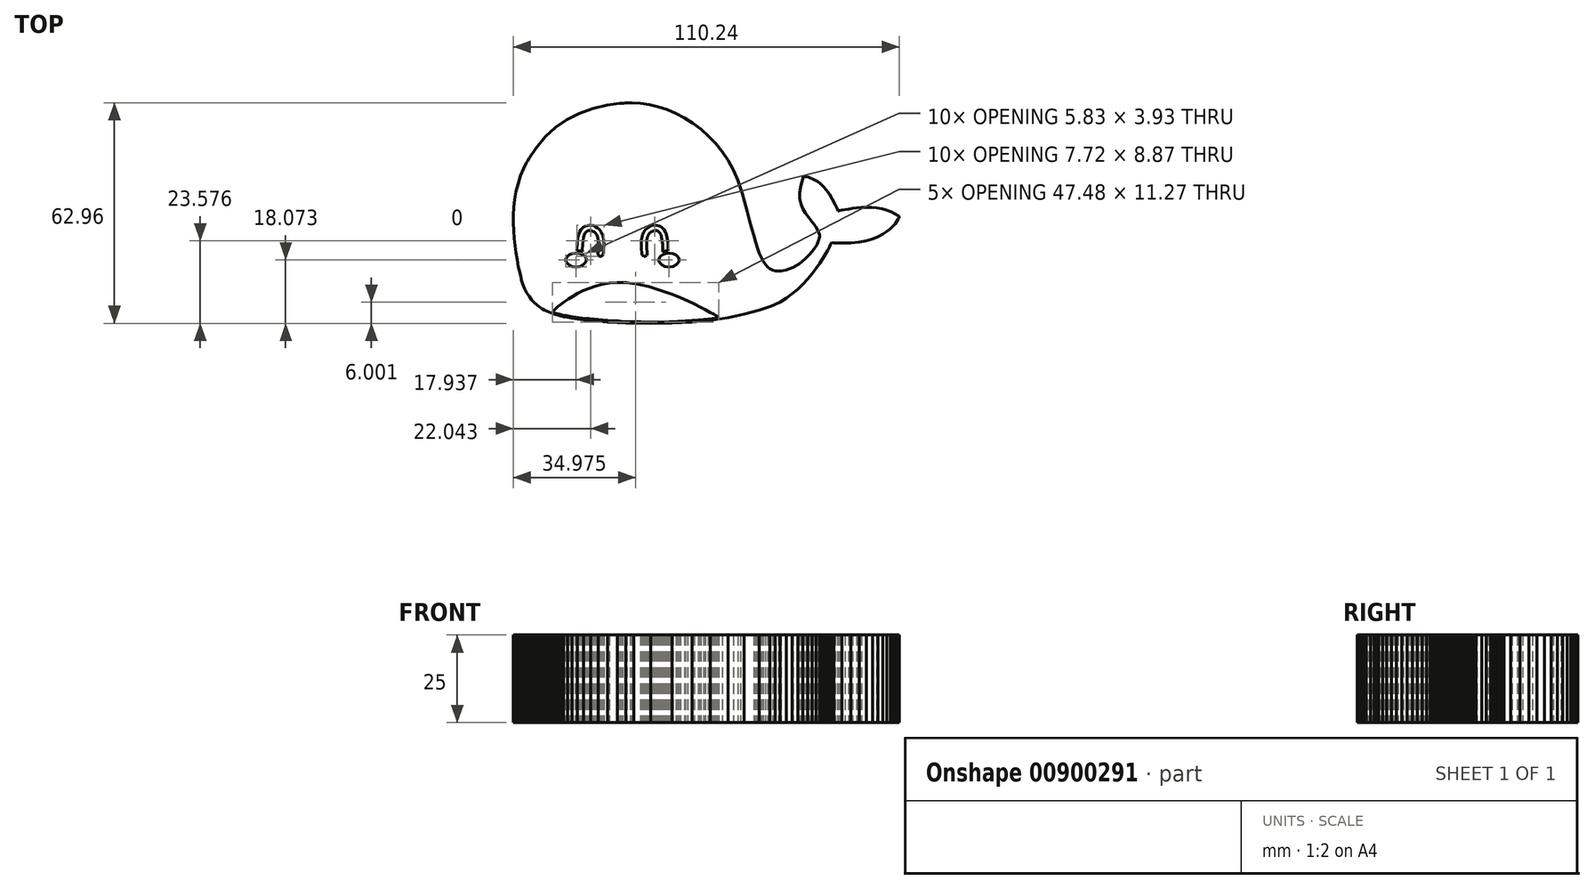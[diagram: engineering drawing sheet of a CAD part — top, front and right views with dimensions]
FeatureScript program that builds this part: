
annotation { "Feature Type Name" : "Feature", "Feature Type Description" : "" }
export const myFeature = defineFeature(function(context is Context, id is Id, definition is map)
    precondition{}
    {
        {
            var Q0;
            Q0=qCreatedBy(makeId("Top.planeOp"),FACE);
            var sketch = newSketch(context, id + "F0", { "sketchPlane" : qUnion([Q0])});
            skLineSegment(sketch, "E0", {"start": v(-43.89, -35.84) * mm, "end": v(-43.96, -35.82) * mm});
            skLineSegment(sketch, "E1", {"start": v(-43.96, -35.82) * mm, "end": v(-44.19, -35.76) * mm});
            skLineSegment(sketch, "E2", {"start": v(-44.19, -35.76) * mm, "end": v(-44.54, -35.65) * mm});
            skLineSegment(sketch, "E3", {"start": v(-44.54, -35.65) * mm, "end": v(-45, -35.48) * mm});
            skLineSegment(sketch, "E4", {"start": v(-45, -35.48) * mm, "end": v(-45.55, -35.25) * mm});
            skLineSegment(sketch, "E5", {"start": v(-45.55, -35.25) * mm, "end": v(-46.18, -34.93) * mm});
            skLineSegment(sketch, "E6", {"start": v(-46.18, -34.93) * mm, "end": v(-46.87, -34.54) * mm});
            skLineSegment(sketch, "E7", {"start": v(-46.87, -34.54) * mm, "end": v(-47.6, -34.06) * mm});
            skLineSegment(sketch, "E8", {"start": v(-47.6, -34.06) * mm, "end": v(-48.35, -33.47) * mm});
            skLineSegment(sketch, "E9", {"start": v(-48.35, -33.47) * mm, "end": v(-49.11, -32.78) * mm});
            skLineSegment(sketch, "E10", {"start": v(-49.11, -32.78) * mm, "end": v(-49.86, -31.97) * mm});
            skLineSegment(sketch, "E11", {"start": v(-49.86, -31.97) * mm, "end": v(-50.59, -31.03) * mm});
            skLineSegment(sketch, "E12", {"start": v(-50.59, -31.03) * mm, "end": v(-51.27, -29.97) * mm});
            skLineSegment(sketch, "E13", {"start": v(-51.27, -29.97) * mm, "end": v(-51.89, -28.76) * mm});
            skLineSegment(sketch, "E14", {"start": v(-51.89, -28.76) * mm, "end": v(-52.43, -27.4) * mm});
            skLineSegment(sketch, "E15", {"start": v(-52.43, -27.4) * mm, "end": v(-52.78, -26.28) * mm});
            skLineSegment(sketch, "E16", {"start": v(-52.78, -26.28) * mm, "end": v(-52.87, -25.9) * mm});
            skLineSegment(sketch, "E17", {"start": v(-52.87, -25.9) * mm, "end": v(-52.97, -25.48) * mm});
            skLineSegment(sketch, "E18", {"start": v(-52.97, -25.48) * mm, "end": v(-53.26, -24.24) * mm});
            skLineSegment(sketch, "E19", {"start": v(-53.26, -24.24) * mm, "end": v(-53.65, -22.46) * mm});
            skLineSegment(sketch, "E20", {"start": v(-53.65, -22.46) * mm, "end": v(-54.02, -20.58) * mm});
            skLineSegment(sketch, "E21", {"start": v(-54.02, -20.58) * mm, "end": v(-54.36, -18.6) * mm});
            skLineSegment(sketch, "E22", {"start": v(-54.36, -18.6) * mm, "end": v(-54.65, -16.55) * mm});
            skLineSegment(sketch, "E23", {"start": v(-54.65, -16.55) * mm, "end": v(-54.88, -14.43) * mm});
            skLineSegment(sketch, "E24", {"start": v(-54.88, -14.43) * mm, "end": v(-55.04, -12.26) * mm});
            skLineSegment(sketch, "E25", {"start": v(-55.04, -12.26) * mm, "end": v(-55.12, -10.05) * mm});
            skLineSegment(sketch, "E26", {"start": v(-55.12, -10.05) * mm, "end": v(-55.1, -7.8) * mm});
            skLineSegment(sketch, "E27", {"start": v(-55.1, -7.8) * mm, "end": v(-54.96, -5.55) * mm});
            skLineSegment(sketch, "E28", {"start": v(-54.96, -5.55) * mm, "end": v(-54.7, -3.3) * mm});
            skLineSegment(sketch, "E29", {"start": v(-54.7, -3.3) * mm, "end": v(-54.32, -1.05) * mm});
            skLineSegment(sketch, "E30", {"start": v(-54.32, -1.05) * mm, "end": v(-53.77, 1.17) * mm});
            skLineSegment(sketch, "E31", {"start": v(-53.77, 1.17) * mm, "end": v(-53.06, 3.35) * mm});
            skLineSegment(sketch, "E32", {"start": v(-53.06, 3.35) * mm, "end": v(-52.18, 5.48) * mm});
            skLineSegment(sketch, "E33", {"start": v(-52.18, 5.48) * mm, "end": v(-51.4, 7.05) * mm});
            skLineSegment(sketch, "E34", {"start": v(-51.4, 7.05) * mm, "end": v(-51.1, 7.55) * mm});
            skLineSegment(sketch, "E35", {"start": v(-51.1, 7.55) * mm, "end": v(-50.54, 8.52) * mm});
            skLineSegment(sketch, "E36", {"start": v(-50.54, 8.52) * mm, "end": v(-48.66, 11.33) * mm});
            skLineSegment(sketch, "E37", {"start": v(-48.66, 11.33) * mm, "end": v(-45.98, 14.55) * mm});
            skLineSegment(sketch, "E38", {"start": v(-45.98, 14.55) * mm, "end": v(-43.05, 17.26) * mm});
            skLineSegment(sketch, "E39", {"start": v(-43.05, 17.26) * mm, "end": v(-39.84, 19.48) * mm});
            skLineSegment(sketch, "E40", {"start": v(-39.84, 19.48) * mm, "end": v(-36.32, 21.24) * mm});
            skLineSegment(sketch, "E41", {"start": v(-36.32, 21.24) * mm, "end": v(-32.47, 22.6) * mm});
            skLineSegment(sketch, "E42", {"start": v(-32.47, 22.6) * mm, "end": v(-28.27, 23.55) * mm});
            skLineSegment(sketch, "E43", {"start": v(-28.27, 23.55) * mm, "end": v(-24.82, 24.06) * mm});
            skLineSegment(sketch, "E44", {"start": v(-24.82, 24.06) * mm, "end": v(-23.67, 24.16) * mm});
            skLineSegment(sketch, "E45", {"start": v(-23.67, 24.16) * mm, "end": v(-23.07, 24.22) * mm});
            skLineSegment(sketch, "E46", {"start": v(-23.07, 24.22) * mm, "end": v(-21.23, 24.26) * mm});
            skLineSegment(sketch, "E47", {"start": v(-21.23, 24.26) * mm, "end": v(-18.74, 24.12) * mm});
            skLineSegment(sketch, "E48", {"start": v(-18.74, 24.12) * mm, "end": v(-16.21, 23.74) * mm});
            skLineSegment(sketch, "E49", {"start": v(-16.21, 23.74) * mm, "end": v(-13.67, 23.12) * mm});
            skLineSegment(sketch, "E50", {"start": v(-13.67, 23.12) * mm, "end": v(-11.14, 22.28) * mm});
            skLineSegment(sketch, "E51", {"start": v(-11.14, 22.28) * mm, "end": v(-8.64, 21.2) * mm});
            skLineSegment(sketch, "E52", {"start": v(-8.64, 21.2) * mm, "end": v(-6.2, 19.92) * mm});
            skLineSegment(sketch, "E53", {"start": v(-6.2, 19.92) * mm, "end": v(-3.82, 18.41) * mm});
            skLineSegment(sketch, "E54", {"start": v(-3.82, 18.41) * mm, "end": v(-1.54, 16.7) * mm});
            skLineSegment(sketch, "E55", {"start": v(-1.54, 16.7) * mm, "end": v(0.63, 14.77) * mm});
            skLineSegment(sketch, "E56", {"start": v(0.63, 14.77) * mm, "end": v(2.66, 12.64) * mm});
            skLineSegment(sketch, "E57", {"start": v(2.66, 12.64) * mm, "end": v(4.53, 10.32) * mm});
            skLineSegment(sketch, "E58", {"start": v(4.53, 10.32) * mm, "end": v(6.22, 7.8) * mm});
            skLineSegment(sketch, "E59", {"start": v(6.22, 7.8) * mm, "end": v(7.72, 5.1) * mm});
            skLineSegment(sketch, "E60", {"start": v(7.72, 5.1) * mm, "end": v(8.99, 2.2) * mm});
            skLineSegment(sketch, "E61", {"start": v(8.99, 2.2) * mm, "end": v(9.8, -0.09) * mm});
            skLineSegment(sketch, "E62", {"start": v(9.8, -0.09) * mm, "end": v(10.02, -0.87) * mm});
            skLineSegment(sketch, "E63", {"start": v(10.02, -0.87) * mm, "end": v(10.24, -1.62) * mm});
            skLineSegment(sketch, "E64", {"start": v(10.24, -1.62) * mm, "end": v(10.87, -3.9) * mm});
            skLineSegment(sketch, "E65", {"start": v(10.87, -3.9) * mm, "end": v(11.64, -6.69) * mm});
            skLineSegment(sketch, "E66", {"start": v(11.64, -6.69) * mm, "end": v(12.33, -9.24) * mm});
            skLineSegment(sketch, "E67", {"start": v(12.33, -9.24) * mm, "end": v(12.96, -11.56) * mm});
            skLineSegment(sketch, "E68", {"start": v(12.96, -11.56) * mm, "end": v(13.55, -13.65) * mm});
            skLineSegment(sketch, "E69", {"start": v(13.55, -13.65) * mm, "end": v(14.1, -15.53) * mm});
            skLineSegment(sketch, "E70", {"start": v(14.1, -15.53) * mm, "end": v(14.63, -17.2) * mm});
            skLineSegment(sketch, "E71", {"start": v(14.63, -17.2) * mm, "end": v(15.15, -18.65) * mm});
            skLineSegment(sketch, "E72", {"start": v(15.15, -18.65) * mm, "end": v(15.69, -19.92) * mm});
            skLineSegment(sketch, "E73", {"start": v(15.69, -19.92) * mm, "end": v(16.24, -20.99) * mm});
            skLineSegment(sketch, "E74", {"start": v(16.24, -20.99) * mm, "end": v(16.83, -21.88) * mm});
            skLineSegment(sketch, "E75", {"start": v(16.83, -21.88) * mm, "end": v(17.47, -22.6) * mm});
            skLineSegment(sketch, "E76", {"start": v(17.47, -22.6) * mm, "end": v(18.16, -23.13) * mm});
            skLineSegment(sketch, "E77", {"start": v(18.16, -23.13) * mm, "end": v(18.94, -23.51) * mm});
            skLineSegment(sketch, "E78", {"start": v(18.94, -23.51) * mm, "end": v(19.8, -23.73) * mm});
            skLineSegment(sketch, "E79", {"start": v(19.8, -23.73) * mm, "end": v(20.53, -23.8) * mm});
            skLineSegment(sketch, "E80", {"start": v(20.53, -23.8) * mm, "end": v(20.77, -23.8) * mm});
            skLineSegment(sketch, "E81", {"start": v(20.77, -23.8) * mm, "end": v(21.28, -23.8) * mm});
            skLineSegment(sketch, "E82", {"start": v(21.28, -23.8) * mm, "end": v(22.8, -23.53) * mm});
            skLineSegment(sketch, "E83", {"start": v(22.8, -23.53) * mm, "end": v(24.75, -22.77) * mm});
            skLineSegment(sketch, "E84", {"start": v(24.75, -22.77) * mm, "end": v(26.57, -21.67) * mm});
            skLineSegment(sketch, "E85", {"start": v(26.57, -21.67) * mm, "end": v(28.22, -20.34) * mm});
            skLineSegment(sketch, "E86", {"start": v(28.22, -20.34) * mm, "end": v(29.64, -18.92) * mm});
            skLineSegment(sketch, "E87", {"start": v(29.64, -18.92) * mm, "end": v(30.78, -17.52) * mm});
            skLineSegment(sketch, "E88", {"start": v(30.78, -17.52) * mm, "end": v(31.58, -16.27) * mm});
            skLineSegment(sketch, "E89", {"start": v(31.58, -16.27) * mm, "end": v(31.93, -15.56) * mm});
            skLineSegment(sketch, "E90", {"start": v(31.93, -15.56) * mm, "end": v(32, -15.3) * mm});
            skLineSegment(sketch, "E91", {"start": v(32, -15.3) * mm, "end": v(32.03, -15.2) * mm});
            skLineSegment(sketch, "E92", {"start": v(32.03, -15.2) * mm, "end": v(32.14, -14.86) * mm});
            skLineSegment(sketch, "E93", {"start": v(32.14, -14.86) * mm, "end": v(32.27, -14.43) * mm});
            skLineSegment(sketch, "E94", {"start": v(32.27, -14.43) * mm, "end": v(32.35, -13.98) * mm});
            skLineSegment(sketch, "E95", {"start": v(32.35, -13.98) * mm, "end": v(32.33, -13.45) * mm});
            skLineSegment(sketch, "E96", {"start": v(32.33, -13.45) * mm, "end": v(32.17, -12.81) * mm});
            skLineSegment(sketch, "E97", {"start": v(32.17, -12.81) * mm, "end": v(31.8, -12.01) * mm});
            skLineSegment(sketch, "E98", {"start": v(31.8, -12.01) * mm, "end": v(31.19, -11.01) * mm});
            skLineSegment(sketch, "E99", {"start": v(31.19, -11.01) * mm, "end": v(30.52, -10.07) * mm});
            skLineSegment(sketch, "E100", {"start": v(30.52, -10.07) * mm, "end": v(30.29, -9.76) * mm});
            skLineSegment(sketch, "E101", {"start": v(30.29, -9.76) * mm, "end": v(30.03, -9.43) * mm});
            skLineSegment(sketch, "E102", {"start": v(30.03, -9.43) * mm, "end": v(29.26, -8.44) * mm});
            skLineSegment(sketch, "E103", {"start": v(29.26, -8.44) * mm, "end": v(28.34, -7.2) * mm});
            skLineSegment(sketch, "E104", {"start": v(28.34, -7.2) * mm, "end": v(27.59, -5.95) * mm});
            skLineSegment(sketch, "E105", {"start": v(27.59, -5.95) * mm, "end": v(27.03, -4.62) * mm});
            skLineSegment(sketch, "E106", {"start": v(27.03, -4.62) * mm, "end": v(26.72, -3.12) * mm});
            skLineSegment(sketch, "E107", {"start": v(26.72, -3.12) * mm, "end": v(26.7, -1.38) * mm});
            skLineSegment(sketch, "E108", {"start": v(26.7, -1.38) * mm, "end": v(27.02, 0.7) * mm});
            skLineSegment(sketch, "E109", {"start": v(27.02, 0.7) * mm, "end": v(27.52, 2.57) * mm});
            skLineSegment(sketch, "E110", {"start": v(27.52, 2.57) * mm, "end": v(27.72, 3.19) * mm});
            skLineSegment(sketch, "E111", {"start": v(27.72, 3.19) * mm, "end": v(27.79, 3.2) * mm});
            skLineSegment(sketch, "E112", {"start": v(27.79, 3.2) * mm, "end": v(27.98, 3.2) * mm});
            skLineSegment(sketch, "E113", {"start": v(27.98, 3.2) * mm, "end": v(28.28, 3.18) * mm});
            skLineSegment(sketch, "E114", {"start": v(28.28, 3.18) * mm, "end": v(28.69, 3.12) * mm});
            skLineSegment(sketch, "E115", {"start": v(28.69, 3.12) * mm, "end": v(29.19, 3.02) * mm});
            skLineSegment(sketch, "E116", {"start": v(29.19, 3.02) * mm, "end": v(29.76, 2.84) * mm});
            skLineSegment(sketch, "E117", {"start": v(29.76, 2.84) * mm, "end": v(30.41, 2.57) * mm});
            skLineSegment(sketch, "E118", {"start": v(30.41, 2.57) * mm, "end": v(31.12, 2.2) * mm});
            skLineSegment(sketch, "E119", {"start": v(31.12, 2.2) * mm, "end": v(31.88, 1.7) * mm});
            skLineSegment(sketch, "E120", {"start": v(31.88, 1.7) * mm, "end": v(32.67, 1.07) * mm});
            skLineSegment(sketch, "E121", {"start": v(32.67, 1.07) * mm, "end": v(33.5, 0.28) * mm});
            skLineSegment(sketch, "E122", {"start": v(33.5, 0.28) * mm, "end": v(34.33, -0.69) * mm});
            skLineSegment(sketch, "E123", {"start": v(34.33, -0.69) * mm, "end": v(35.17, -1.84) * mm});
            skLineSegment(sketch, "E124", {"start": v(35.17, -1.84) * mm, "end": v(36, -3.2) * mm});
            skLineSegment(sketch, "E125", {"start": v(36, -3.2) * mm, "end": v(36.82, -4.8) * mm});
            skLineSegment(sketch, "E126", {"start": v(36.82, -4.8) * mm, "end": v(37.43, -6.17) * mm});
            skLineSegment(sketch, "E127", {"start": v(37.43, -6.17) * mm, "end": v(37.61, -6.63) * mm});
            skLineSegment(sketch, "E128", {"start": v(37.61, -6.63) * mm, "end": v(37.75, -6.6) * mm});
            skLineSegment(sketch, "E129", {"start": v(37.75, -6.6) * mm, "end": v(38.14, -6.5) * mm});
            skLineSegment(sketch, "E130", {"start": v(38.14, -6.5) * mm, "end": v(38.77, -6.37) * mm});
            skLineSegment(sketch, "E131", {"start": v(38.77, -6.37) * mm, "end": v(39.59, -6.22) * mm});
            skLineSegment(sketch, "E132", {"start": v(39.59, -6.22) * mm, "end": v(40.58, -6.05) * mm});
            skLineSegment(sketch, "E133", {"start": v(40.58, -6.05) * mm, "end": v(41.73, -5.9) * mm});
            skLineSegment(sketch, "E134", {"start": v(41.73, -5.9) * mm, "end": v(42.99, -5.76) * mm});
            skLineSegment(sketch, "E135", {"start": v(42.99, -5.76) * mm, "end": v(44.34, -5.66) * mm});
            skLineSegment(sketch, "E136", {"start": v(44.34, -5.66) * mm, "end": v(45.75, -5.62) * mm});
            skLineSegment(sketch, "E137", {"start": v(45.75, -5.62) * mm, "end": v(47.2, -5.66) * mm});
            skLineSegment(sketch, "E138", {"start": v(47.2, -5.66) * mm, "end": v(48.66, -5.78) * mm});
            skLineSegment(sketch, "E139", {"start": v(48.66, -5.78) * mm, "end": v(50.1, -6) * mm});
            skLineSegment(sketch, "E140", {"start": v(50.1, -6) * mm, "end": v(51.5, -6.35) * mm});
            skLineSegment(sketch, "E141", {"start": v(51.5, -6.35) * mm, "end": v(52.81, -6.83) * mm});
            skLineSegment(sketch, "E142", {"start": v(52.81, -6.83) * mm, "end": v(54.03, -7.46) * mm});
            skLineSegment(sketch, "E143", {"start": v(54.03, -7.46) * mm, "end": v(54.86, -8.05) * mm});
            skLineSegment(sketch, "E144", {"start": v(54.86, -8.05) * mm, "end": v(55.12, -8.27) * mm});
            skLineSegment(sketch, "E145", {"start": v(55.12, -8.27) * mm, "end": v(55.08, -8.37) * mm});
            skLineSegment(sketch, "E146", {"start": v(55.08, -8.37) * mm, "end": v(54.96, -8.64) * mm});
            skLineSegment(sketch, "E147", {"start": v(54.96, -8.64) * mm, "end": v(54.73, -9.07) * mm});
            skLineSegment(sketch, "E148", {"start": v(54.73, -9.07) * mm, "end": v(54.4, -9.62) * mm});
            skLineSegment(sketch, "E149", {"start": v(54.4, -9.62) * mm, "end": v(53.92, -10.27) * mm});
            skLineSegment(sketch, "E150", {"start": v(53.92, -10.27) * mm, "end": v(53.3, -10.99) * mm});
            skLineSegment(sketch, "E151", {"start": v(53.3, -10.99) * mm, "end": v(52.53, -11.74) * mm});
            skLineSegment(sketch, "E152", {"start": v(52.53, -11.74) * mm, "end": v(51.58, -12.5) * mm});
            skLineSegment(sketch, "E153", {"start": v(51.58, -12.5) * mm, "end": v(50.43, -13.25) * mm});
            skLineSegment(sketch, "E154", {"start": v(50.43, -13.25) * mm, "end": v(49.08, -13.95) * mm});
            skLineSegment(sketch, "E155", {"start": v(49.08, -13.95) * mm, "end": v(47.5, -14.58) * mm});
            skLineSegment(sketch, "E156", {"start": v(47.5, -14.58) * mm, "end": v(45.7, -15.11) * mm});
            skLineSegment(sketch, "E157", {"start": v(45.7, -15.11) * mm, "end": v(43.63, -15.51) * mm});
            skLineSegment(sketch, "E158", {"start": v(43.63, -15.51) * mm, "end": v(41.3, -15.76) * mm});
            skLineSegment(sketch, "E159", {"start": v(41.3, -15.76) * mm, "end": v(38.68, -15.82) * mm});
            skLineSegment(sketch, "E160", {"start": v(38.68, -15.82) * mm, "end": v(36.5, -15.73) * mm});
            skLineSegment(sketch, "E161", {"start": v(36.5, -15.73) * mm, "end": v(35.76, -15.67) * mm});
            skLineSegment(sketch, "E162", {"start": v(35.76, -15.67) * mm, "end": v(35.7, -15.82) * mm});
            skLineSegment(sketch, "E163", {"start": v(35.7, -15.82) * mm, "end": v(35.47, -16.26) * mm});
            skLineSegment(sketch, "E164", {"start": v(35.47, -16.26) * mm, "end": v(35.12, -16.96) * mm});
            skLineSegment(sketch, "E165", {"start": v(35.12, -16.96) * mm, "end": v(34.62, -17.87) * mm});
            skLineSegment(sketch, "E166", {"start": v(34.62, -17.87) * mm, "end": v(34, -18.96) * mm});
            skLineSegment(sketch, "E167", {"start": v(34, -18.96) * mm, "end": v(33.23, -20.2) * mm});
            skLineSegment(sketch, "E168", {"start": v(33.23, -20.2) * mm, "end": v(32.34, -21.57) * mm});
            skLineSegment(sketch, "E169", {"start": v(32.34, -21.57) * mm, "end": v(31.33, -23.02) * mm});
            skLineSegment(sketch, "E170", {"start": v(31.33, -23.02) * mm, "end": v(30.2, -24.51) * mm});
            skLineSegment(sketch, "E171", {"start": v(30.2, -24.51) * mm, "end": v(28.95, -26.02) * mm});
            skLineSegment(sketch, "E172", {"start": v(28.95, -26.02) * mm, "end": v(27.58, -27.51) * mm});
            skLineSegment(sketch, "E173", {"start": v(27.58, -27.51) * mm, "end": v(26.1, -28.95) * mm});
            skLineSegment(sketch, "E174", {"start": v(26.1, -28.95) * mm, "end": v(24.52, -30.3) * mm});
            skLineSegment(sketch, "E175", {"start": v(24.52, -30.3) * mm, "end": v(22.84, -31.54) * mm});
            skLineSegment(sketch, "E176", {"start": v(22.84, -31.54) * mm, "end": v(21.05, -32.61) * mm});
            skLineSegment(sketch, "E177", {"start": v(21.05, -32.61) * mm, "end": v(19.64, -33.3) * mm});
            skLineSegment(sketch, "E178", {"start": v(19.64, -33.3) * mm, "end": v(19.16, -33.5) * mm});
            skLineSegment(sketch, "E179", {"start": v(19.16, -33.5) * mm, "end": v(18.17, -33.9) * mm});
            skLineSegment(sketch, "E180", {"start": v(18.17, -33.9) * mm, "end": v(15.14, -34.94) * mm});
            skLineSegment(sketch, "E181", {"start": v(15.14, -34.94) * mm, "end": v(10.82, -36.13) * mm});
            skLineSegment(sketch, "E182", {"start": v(10.82, -36.13) * mm, "end": v(6.17, -37.09) * mm});
            skLineSegment(sketch, "E183", {"start": v(6.17, -37.09) * mm, "end": v(1.2, -37.81) * mm});
            skLineSegment(sketch, "E184", {"start": v(1.2, -37.81) * mm, "end": v(-4.12, -38.32) * mm});
            skLineSegment(sketch, "E185", {"start": v(-4.12, -38.32) * mm, "end": v(-9.8, -38.6) * mm});
            skLineSegment(sketch, "E186", {"start": v(-9.8, -38.6) * mm, "end": v(-15.83, -38.7) * mm});
            skLineSegment(sketch, "E187", {"start": v(-15.83, -38.7) * mm, "end": v(-20.65, -38.64) * mm});
            skLineSegment(sketch, "E188", {"start": v(-20.65, -38.64) * mm, "end": v(-22.25, -38.6) * mm});
            skLineSegment(sketch, "E189", {"start": v(-22.25, -38.6) * mm, "end": v(-23.04, -38.57) * mm});
            skLineSegment(sketch, "E190", {"start": v(-23.04, -38.57) * mm, "end": v(-25.4, -38.48) * mm});
            skLineSegment(sketch, "E191", {"start": v(-25.4, -38.48) * mm, "end": v(-28.25, -38.33) * mm});
            skLineSegment(sketch, "E192", {"start": v(-28.25, -38.33) * mm, "end": v(-30.8, -38.15) * mm});
            skLineSegment(sketch, "E193", {"start": v(-30.8, -38.15) * mm, "end": v(-33.07, -37.95) * mm});
            skLineSegment(sketch, "E194", {"start": v(-33.07, -37.95) * mm, "end": v(-35.08, -37.73) * mm});
            skLineSegment(sketch, "E195", {"start": v(-35.08, -37.73) * mm, "end": v(-36.85, -37.5) * mm});
            skLineSegment(sketch, "E196", {"start": v(-36.85, -37.5) * mm, "end": v(-38.38, -37.26) * mm});
            skLineSegment(sketch, "E197", {"start": v(-38.38, -37.26) * mm, "end": v(-39.68, -37.02) * mm});
            skLineSegment(sketch, "E198", {"start": v(-39.68, -37.02) * mm, "end": v(-40.78, -36.8) * mm});
            skLineSegment(sketch, "E199", {"start": v(-40.78, -36.8) * mm, "end": v(-41.7, -36.57) * mm});
            skLineSegment(sketch, "E200", {"start": v(-41.7, -36.57) * mm, "end": v(-42.42, -36.37) * mm});
            skLineSegment(sketch, "E201", {"start": v(-42.42, -36.37) * mm, "end": v(-42.99, -36.2) * mm});
            skLineSegment(sketch, "E202", {"start": v(-42.99, -36.2) * mm, "end": v(-43.4, -36.05) * mm});
            skLineSegment(sketch, "E203", {"start": v(-43.4, -36.05) * mm, "end": v(-43.68, -35.94) * mm});
            skLineSegment(sketch, "E204", {"start": v(-43.68, -35.94) * mm, "end": v(-43.84, -35.87) * mm});
            skLineSegment(sketch, "E205", {"start": v(-43.84, -35.87) * mm, "end": v(-43.89, -35.84) * mm});
            skLineSegment(sketch, "E206", {"start": v(-43.89, -35.38) * mm, "end": v(-43.79, -35.28) * mm});
            skLineSegment(sketch, "E207", {"start": v(-43.79, -35.28) * mm, "end": v(-43.5, -35) * mm});
            skLineSegment(sketch, "E208", {"start": v(-43.5, -35) * mm, "end": v(-43.02, -34.56) * mm});
            skLineSegment(sketch, "E209", {"start": v(-43.02, -34.56) * mm, "end": v(-42.36, -33.99) * mm});
            skLineSegment(sketch, "E210", {"start": v(-42.36, -33.99) * mm, "end": v(-41.54, -33.32) * mm});
            skLineSegment(sketch, "E211", {"start": v(-41.54, -33.32) * mm, "end": v(-40.55, -32.57) * mm});
            skLineSegment(sketch, "E212", {"start": v(-40.55, -32.57) * mm, "end": v(-39.4, -31.78) * mm});
            skLineSegment(sketch, "E213", {"start": v(-39.4, -31.78) * mm, "end": v(-38.11, -30.97) * mm});
            skLineSegment(sketch, "E214", {"start": v(-38.11, -30.97) * mm, "end": v(-36.68, -30.17) * mm});
            skLineSegment(sketch, "E215", {"start": v(-36.68, -30.17) * mm, "end": v(-35.12, -29.4) * mm});
            skLineSegment(sketch, "E216", {"start": v(-35.12, -29.4) * mm, "end": v(-33.43, -28.7) * mm});
            skLineSegment(sketch, "E217", {"start": v(-33.43, -28.7) * mm, "end": v(-31.62, -28.1) * mm});
            skLineSegment(sketch, "E218", {"start": v(-31.62, -28.1) * mm, "end": v(-29.7, -27.6) * mm});
            skLineSegment(sketch, "E219", {"start": v(-29.7, -27.6) * mm, "end": v(-27.67, -27.25) * mm});
            skLineSegment(sketch, "E220", {"start": v(-27.67, -27.25) * mm, "end": v(-25.55, -27.07) * mm});
            skLineSegment(sketch, "E221", {"start": v(-25.55, -27.07) * mm, "end": v(-23.9, -27.06) * mm});
            skLineSegment(sketch, "E222", {"start": v(-23.9, -27.06) * mm, "end": v(-23.35, -27.1) * mm});
            skLineSegment(sketch, "E223", {"start": v(-23.35, -27.1) * mm, "end": v(-22.78, -27.13) * mm});
            skLineSegment(sketch, "E224", {"start": v(-22.78, -27.13) * mm, "end": v(-21.07, -27.32) * mm});
            skLineSegment(sketch, "E225", {"start": v(-21.07, -27.32) * mm, "end": v(-18.75, -27.72) * mm});
            skLineSegment(sketch, "E226", {"start": v(-18.75, -27.72) * mm, "end": v(-16.4, -28.27) * mm});
            skLineSegment(sketch, "E227", {"start": v(-16.4, -28.27) * mm, "end": v(-14.08, -28.94) * mm});
            skLineSegment(sketch, "E228", {"start": v(-14.08, -28.94) * mm, "end": v(-11.78, -29.7) * mm});
            skLineSegment(sketch, "E229", {"start": v(-11.78, -29.7) * mm, "end": v(-9.55, -30.53) * mm});
            skLineSegment(sketch, "E230", {"start": v(-9.55, -30.53) * mm, "end": v(-7.4, -31.4) * mm});
            skLineSegment(sketch, "E231", {"start": v(-7.4, -31.4) * mm, "end": v(-5.38, -32.3) * mm});
            skLineSegment(sketch, "E232", {"start": v(-5.38, -32.3) * mm, "end": v(-3.49, -33.19) * mm});
            skLineSegment(sketch, "E233", {"start": v(-3.49, -33.19) * mm, "end": v(-1.77, -34.04) * mm});
            skLineSegment(sketch, "E234", {"start": v(-1.77, -34.04) * mm, "end": v(-0.24, -34.83) * mm});
            skLineSegment(sketch, "E235", {"start": v(-0.24, -34.83) * mm, "end": v(1.07, -35.53) * mm});
            skLineSegment(sketch, "E236", {"start": v(1.07, -35.53) * mm, "end": v(2.14, -36.13) * mm});
            skLineSegment(sketch, "E237", {"start": v(2.14, -36.13) * mm, "end": v(2.93, -36.58) * mm});
            skLineSegment(sketch, "E238", {"start": v(2.93, -36.58) * mm, "end": v(3.43, -36.87) * mm});
            skLineSegment(sketch, "E239", {"start": v(3.43, -36.87) * mm, "end": v(3.6, -36.98) * mm});
            skLineSegment(sketch, "E240", {"start": v(3.6, -36.98) * mm, "end": v(3.47, -37) * mm});
            skLineSegment(sketch, "E241", {"start": v(3.47, -37) * mm, "end": v(3.1, -37.07) * mm});
            skLineSegment(sketch, "E242", {"start": v(3.1, -37.07) * mm, "end": v(2.48, -37.17) * mm});
            skLineSegment(sketch, "E243", {"start": v(2.48, -37.17) * mm, "end": v(1.63, -37.3) * mm});
            skLineSegment(sketch, "E244", {"start": v(1.63, -37.3) * mm, "end": v(0.55, -37.44) * mm});
            skLineSegment(sketch, "E245", {"start": v(0.55, -37.44) * mm, "end": v(-0.76, -37.6) * mm});
            skLineSegment(sketch, "E246", {"start": v(-0.76, -37.6) * mm, "end": v(-2.3, -37.75) * mm});
            skLineSegment(sketch, "E247", {"start": v(-2.3, -37.75) * mm, "end": v(-4.04, -37.9) * mm});
            skLineSegment(sketch, "E248", {"start": v(-4.04, -37.9) * mm, "end": v(-5.99, -38.05) * mm});
            skLineSegment(sketch, "E249", {"start": v(-5.99, -38.05) * mm, "end": v(-8.14, -38.17) * mm});
            skLineSegment(sketch, "E250", {"start": v(-8.14, -38.17) * mm, "end": v(-10.5, -38.26) * mm});
            skLineSegment(sketch, "E251", {"start": v(-10.5, -38.26) * mm, "end": v(-13.03, -38.32) * mm});
            skLineSegment(sketch, "E252", {"start": v(-13.03, -38.32) * mm, "end": v(-15.76, -38.33) * mm});
            skLineSegment(sketch, "E253", {"start": v(-15.76, -38.33) * mm, "end": v(-18.67, -38.3) * mm});
            skLineSegment(sketch, "E254", {"start": v(-18.67, -38.3) * mm, "end": v(-21.75, -38.2) * mm});
            skLineSegment(sketch, "E255", {"start": v(-21.75, -38.2) * mm, "end": v(-24.2, -38.09) * mm});
            skLineSegment(sketch, "E256", {"start": v(-24.2, -38.09) * mm, "end": v(-25, -38.04) * mm});
            skLineSegment(sketch, "E257", {"start": v(-25, -38.04) * mm, "end": v(-25.79, -38) * mm});
            skLineSegment(sketch, "E258", {"start": v(-25.79, -38) * mm, "end": v(-28.15, -37.83) * mm});
            skLineSegment(sketch, "E259", {"start": v(-28.15, -37.83) * mm, "end": v(-30.92, -37.62) * mm});
            skLineSegment(sketch, "E260", {"start": v(-30.92, -37.62) * mm, "end": v(-33.35, -37.4) * mm});
            skLineSegment(sketch, "E261", {"start": v(-33.35, -37.4) * mm, "end": v(-35.46, -37.17) * mm});
            skLineSegment(sketch, "E262", {"start": v(-35.46, -37.17) * mm, "end": v(-37.26, -36.95) * mm});
            skLineSegment(sketch, "E263", {"start": v(-37.26, -36.95) * mm, "end": v(-38.8, -36.73) * mm});
            skLineSegment(sketch, "E264", {"start": v(-38.8, -36.73) * mm, "end": v(-40.07, -36.52) * mm});
            skLineSegment(sketch, "E265", {"start": v(-40.07, -36.52) * mm, "end": v(-41.11, -36.31) * mm});
            skLineSegment(sketch, "E266", {"start": v(-41.11, -36.31) * mm, "end": v(-41.95, -36.12) * mm});
            skLineSegment(sketch, "E267", {"start": v(-41.95, -36.12) * mm, "end": v(-42.6, -35.94) * mm});
            skLineSegment(sketch, "E268", {"start": v(-42.6, -35.94) * mm, "end": v(-43.09, -35.78) * mm});
            skLineSegment(sketch, "E269", {"start": v(-43.09, -35.78) * mm, "end": v(-43.44, -35.65) * mm});
            skLineSegment(sketch, "E270", {"start": v(-43.44, -35.65) * mm, "end": v(-43.67, -35.53) * mm});
            skLineSegment(sketch, "E271", {"start": v(-43.67, -35.53) * mm, "end": v(-43.8, -35.45) * mm});
            skLineSegment(sketch, "E272", {"start": v(-43.8, -35.45) * mm, "end": v(-43.87, -35.4) * mm});
            skLineSegment(sketch, "E273", {"start": v(-43.87, -35.4) * mm, "end": v(-43.89, -35.38) * mm});
            skLineSegment(sketch, "E274", {"start": v(-10.64, -18.66) * mm, "end": v(-10.7, -18.66) * mm});
            skLineSegment(sketch, "E275", {"start": v(-10.7, -18.66) * mm, "end": v(-10.88, -18.67) * mm});
            skLineSegment(sketch, "E276", {"start": v(-10.88, -18.67) * mm, "end": v(-10.9, -18.67) * mm});
            skLineSegment(sketch, "E277", {"start": v(-10.9, -18.67) * mm, "end": v(-11.05, -18.68) * mm});
            skLineSegment(sketch, "E278", {"start": v(-11.05, -18.68) * mm, "end": v(-11.75, -18.8) * mm});
            skLineSegment(sketch, "E279", {"start": v(-11.75, -18.8) * mm, "end": v(-12.36, -19.04) * mm});
            skLineSegment(sketch, "E280", {"start": v(-12.36, -19.04) * mm, "end": v(-12.47, -19.1) * mm});
            skLineSegment(sketch, "E281", {"start": v(-12.47, -19.1) * mm, "end": v(-12.59, -19.16) * mm});
            skLineSegment(sketch, "E282", {"start": v(-12.59, -19.16) * mm, "end": v(-12.92, -19.4) * mm});
            skLineSegment(sketch, "E283", {"start": v(-12.92, -19.4) * mm, "end": v(-13.26, -19.77) * mm});
            skLineSegment(sketch, "E284", {"start": v(-13.26, -19.77) * mm, "end": v(-13.48, -20.18) * mm});
            skLineSegment(sketch, "E285", {"start": v(-13.48, -20.18) * mm, "end": v(-13.56, -20.51) * mm});
            skLineSegment(sketch, "E286", {"start": v(-13.56, -20.51) * mm, "end": v(-13.56, -20.63) * mm});
            skLineSegment(sketch, "E287", {"start": v(-13.56, -20.63) * mm, "end": v(-13.56, -20.82) * mm});
            skLineSegment(sketch, "E288", {"start": v(-13.56, -20.82) * mm, "end": v(-13.33, -21.4) * mm});
            skLineSegment(sketch, "E289", {"start": v(-13.33, -21.4) * mm, "end": v(-12.7, -22.02) * mm});
            skLineSegment(sketch, "E290", {"start": v(-12.7, -22.02) * mm, "end": v(-11.78, -22.44) * mm});
            skLineSegment(sketch, "E291", {"start": v(-11.78, -22.44) * mm, "end": v(-10.93, -22.6) * mm});
            skLineSegment(sketch, "E292", {"start": v(-10.93, -22.6) * mm, "end": v(-10.64, -22.6) * mm});
            skLineSegment(sketch, "E293", {"start": v(-10.64, -22.6) * mm, "end": v(-10.36, -22.6) * mm});
            skLineSegment(sketch, "E294", {"start": v(-10.36, -22.6) * mm, "end": v(-9.5, -22.44) * mm});
            skLineSegment(sketch, "E295", {"start": v(-9.5, -22.44) * mm, "end": v(-8.58, -22.02) * mm});
            skLineSegment(sketch, "E296", {"start": v(-8.58, -22.02) * mm, "end": v(-7.96, -21.4) * mm});
            skLineSegment(sketch, "E297", {"start": v(-7.96, -21.4) * mm, "end": v(-7.73, -20.82) * mm});
            skLineSegment(sketch, "E298", {"start": v(-7.73, -20.82) * mm, "end": v(-7.73, -20.63) * mm});
            skLineSegment(sketch, "E299", {"start": v(-7.73, -20.63) * mm, "end": v(-7.73, -20.44) * mm});
            skLineSegment(sketch, "E300", {"start": v(-7.73, -20.44) * mm, "end": v(-7.96, -19.86) * mm});
            skLineSegment(sketch, "E301", {"start": v(-7.96, -19.86) * mm, "end": v(-8.58, -19.24) * mm});
            skLineSegment(sketch, "E302", {"start": v(-8.58, -19.24) * mm, "end": v(-9.5, -18.82) * mm});
            skLineSegment(sketch, "E303", {"start": v(-9.5, -18.82) * mm, "end": v(-10.36, -18.66) * mm});
            skLineSegment(sketch, "E304", {"start": v(-10.36, -18.66) * mm, "end": v(-10.64, -18.66) * mm});
            skLineSegment(sketch, "E305", {"start": v(-11.4, -13.38) * mm, "end": v(-11.45, -13.18) * mm});
            skLineSegment(sketch, "E306", {"start": v(-11.45, -13.18) * mm, "end": v(-11.67, -12.6) * mm});
            skLineSegment(sketch, "E307", {"start": v(-11.67, -12.6) * mm, "end": v(-12.05, -11.93) * mm});
            skLineSegment(sketch, "E308", {"start": v(-12.05, -11.93) * mm, "end": v(-12.52, -11.4) * mm});
            skLineSegment(sketch, "E309", {"start": v(-12.52, -11.4) * mm, "end": v(-12.94, -11.1) * mm});
            skLineSegment(sketch, "E310", {"start": v(-12.94, -11.1) * mm, "end": v(-13.09, -11.03) * mm});
            skLineSegment(sketch, "E311", {"start": v(-13.09, -11.03) * mm, "end": v(-13.31, -10.92) * mm});
            skLineSegment(sketch, "E312", {"start": v(-13.31, -10.92) * mm, "end": v(-14.5, -10.7) * mm});
            skLineSegment(sketch, "E313", {"start": v(-14.5, -10.7) * mm, "end": v(-15.69, -10.87) * mm});
            skLineSegment(sketch, "E314", {"start": v(-15.69, -10.87) * mm, "end": v(-15.92, -10.97) * mm});
            skLineSegment(sketch, "E315", {"start": v(-15.92, -10.97) * mm, "end": v(-16.12, -11.05) * mm});
            skLineSegment(sketch, "E316", {"start": v(-16.12, -11.05) * mm, "end": v(-16.68, -11.4) * mm});
            skLineSegment(sketch, "E317", {"start": v(-16.68, -11.4) * mm, "end": v(-17.34, -11.99) * mm});
            skLineSegment(sketch, "E318", {"start": v(-17.34, -11.99) * mm, "end": v(-17.86, -12.7) * mm});
            skLineSegment(sketch, "E319", {"start": v(-17.86, -12.7) * mm, "end": v(-18.16, -13.32) * mm});
            skLineSegment(sketch, "E320", {"start": v(-18.16, -13.32) * mm, "end": v(-18.23, -13.53) * mm});
            skLineSegment(sketch, "E321", {"start": v(-18.23, -13.53) * mm, "end": v(-18.34, -13.85) * mm});
            skLineSegment(sketch, "E322", {"start": v(-18.34, -13.85) * mm, "end": v(-18.53, -14.85) * mm});
            skLineSegment(sketch, "E323", {"start": v(-18.53, -14.85) * mm, "end": v(-18.6, -16.2) * mm});
            skLineSegment(sketch, "E324", {"start": v(-18.6, -16.2) * mm, "end": v(-18.55, -17.53) * mm});
            skLineSegment(sketch, "E325", {"start": v(-18.55, -17.53) * mm, "end": v(-18.45, -18.5) * mm});
            skLineSegment(sketch, "E326", {"start": v(-18.45, -18.5) * mm, "end": v(-18.42, -18.82) * mm});
            skLineSegment(sketch, "E327", {"start": v(-18.42, -18.82) * mm, "end": v(-18.41, -18.87) * mm});
            skLineSegment(sketch, "E328", {"start": v(-18.41, -18.87) * mm, "end": v(-18.4, -18.94) * mm});
            skLineSegment(sketch, "E329", {"start": v(-18.4, -18.94) * mm, "end": v(-18.33, -19.15) * mm});
            skLineSegment(sketch, "E330", {"start": v(-18.33, -19.15) * mm, "end": v(-18.16, -19.36) * mm});
            skLineSegment(sketch, "E331", {"start": v(-18.16, -19.36) * mm, "end": v(-17.93, -19.5) * mm});
            skLineSegment(sketch, "E332", {"start": v(-17.93, -19.5) * mm, "end": v(-17.72, -19.56) * mm});
            skLineSegment(sketch, "E333", {"start": v(-17.72, -19.56) * mm, "end": v(-17.65, -19.56) * mm});
            skLineSegment(sketch, "E334", {"start": v(-17.65, -19.56) * mm, "end": v(-17.63, -19.56) * mm});
            skLineSegment(sketch, "E335", {"start": v(-17.63, -19.56) * mm, "end": v(-17.58, -19.55) * mm});
            skLineSegment(sketch, "E336", {"start": v(-17.58, -19.55) * mm, "end": v(-17.57, -19.55) * mm});
            skLineSegment(sketch, "E337", {"start": v(-17.57, -19.55) * mm, "end": v(-17.5, -19.55) * mm});
            skLineSegment(sketch, "E338", {"start": v(-17.5, -19.55) * mm, "end": v(-17.28, -19.46) * mm});
            skLineSegment(sketch, "E339", {"start": v(-17.28, -19.46) * mm, "end": v(-17.06, -19.27) * mm});
            skLineSegment(sketch, "E340", {"start": v(-17.06, -19.27) * mm, "end": v(-16.92, -19.01) * mm});
            skLineSegment(sketch, "E341", {"start": v(-16.92, -19.01) * mm, "end": v(-16.89, -18.79) * mm});
            skLineSegment(sketch, "E342", {"start": v(-16.89, -18.79) * mm, "end": v(-16.9, -18.71) * mm});
            skLineSegment(sketch, "E343", {"start": v(-16.9, -18.71) * mm, "end": v(-16.9, -18.66) * mm});
            skLineSegment(sketch, "E344", {"start": v(-16.9, -18.66) * mm, "end": v(-16.93, -18.36) * mm});
            skLineSegment(sketch, "E345", {"start": v(-16.93, -18.36) * mm, "end": v(-17.02, -17.46) * mm});
            skLineSegment(sketch, "E346", {"start": v(-17.02, -17.46) * mm, "end": v(-17.08, -16.27) * mm});
            skLineSegment(sketch, "E347", {"start": v(-17.08, -16.27) * mm, "end": v(-17.02, -15.1) * mm});
            skLineSegment(sketch, "E348", {"start": v(-17.02, -15.1) * mm, "end": v(-16.87, -14.27) * mm});
            skLineSegment(sketch, "E349", {"start": v(-16.87, -14.27) * mm, "end": v(-16.78, -14) * mm});
            skLineSegment(sketch, "E350", {"start": v(-16.78, -14) * mm, "end": v(-16.74, -13.87) * mm});
            skLineSegment(sketch, "E351", {"start": v(-16.74, -13.87) * mm, "end": v(-16.55, -13.49) * mm});
            skLineSegment(sketch, "E352", {"start": v(-16.55, -13.49) * mm, "end": v(-16.2, -13.03) * mm});
            skLineSegment(sketch, "E353", {"start": v(-16.2, -13.03) * mm, "end": v(-15.8, -12.65) * mm});
            skLineSegment(sketch, "E354", {"start": v(-15.8, -12.65) * mm, "end": v(-15.45, -12.43) * mm});
            skLineSegment(sketch, "E355", {"start": v(-15.45, -12.43) * mm, "end": v(-15.32, -12.38) * mm});
            skLineSegment(sketch, "E356", {"start": v(-15.32, -12.38) * mm, "end": v(-15.25, -12.35) * mm});
            skLineSegment(sketch, "E357", {"start": v(-15.25, -12.35) * mm, "end": v(-15.01, -12.27) * mm});
            skLineSegment(sketch, "E358", {"start": v(-15.01, -12.27) * mm, "end": v(-14.64, -12.22) * mm});
            skLineSegment(sketch, "E359", {"start": v(-14.64, -12.22) * mm, "end": v(-14.22, -12.25) * mm});
            skLineSegment(sketch, "E360", {"start": v(-14.22, -12.25) * mm, "end": v(-13.86, -12.36) * mm});
            skLineSegment(sketch, "E361", {"start": v(-13.86, -12.36) * mm, "end": v(-13.75, -12.41) * mm});
            skLineSegment(sketch, "E362", {"start": v(-13.75, -12.41) * mm, "end": v(-13.66, -12.46) * mm});
            skLineSegment(sketch, "E363", {"start": v(-13.66, -12.46) * mm, "end": v(-13.41, -12.67) * mm});
            skLineSegment(sketch, "E364", {"start": v(-13.41, -12.67) * mm, "end": v(-13.16, -13.03) * mm});
            skLineSegment(sketch, "E365", {"start": v(-13.16, -13.03) * mm, "end": v(-13, -13.41) * mm});
            skLineSegment(sketch, "E366", {"start": v(-13, -13.41) * mm, "end": v(-12.9, -13.67) * mm});
            skLineSegment(sketch, "E367", {"start": v(-12.9, -13.67) * mm, "end": v(-12.89, -13.75) * mm});
            skLineSegment(sketch, "E368", {"start": v(-12.89, -13.75) * mm, "end": v(-12.79, -14.17) * mm});
            skLineSegment(sketch, "E369", {"start": v(-12.79, -14.17) * mm, "end": v(-12.48, -16.13) * mm});
            skLineSegment(sketch, "E370", {"start": v(-12.48, -16.13) * mm, "end": v(-12.44, -17.96) * mm});
            skLineSegment(sketch, "E371", {"start": v(-12.44, -17.96) * mm, "end": v(-12.47, -18.3) * mm});
            skLineSegment(sketch, "E372", {"start": v(-12.47, -18.3) * mm, "end": v(-12.36, -18.24) * mm});
            skLineSegment(sketch, "E373", {"start": v(-12.36, -18.24) * mm, "end": v(-11.75, -18.02) * mm});
            skLineSegment(sketch, "E374", {"start": v(-11.75, -18.02) * mm, "end": v(-11.05, -17.89) * mm});
            skLineSegment(sketch, "E375", {"start": v(-11.05, -17.89) * mm, "end": v(-10.9, -17.88) * mm});
            skLineSegment(sketch, "E376", {"start": v(-10.9, -17.88) * mm, "end": v(-10.9, -17.53) * mm});
            skLineSegment(sketch, "E377", {"start": v(-10.9, -17.53) * mm, "end": v(-10.98, -15.7) * mm});
            skLineSegment(sketch, "E378", {"start": v(-10.98, -15.7) * mm, "end": v(-11.3, -13.78) * mm});
            skLineSegment(sketch, "E379", {"start": v(-11.3, -13.78) * mm, "end": v(-11.4, -13.38) * mm});
            skLineSegment(sketch, "E380", {"start": v(-37.18, -18.66) * mm, "end": v(-37.12, -18.66) * mm});
            skLineSegment(sketch, "E381", {"start": v(-37.12, -18.66) * mm, "end": v(-36.94, -18.67) * mm});
            skLineSegment(sketch, "E382", {"start": v(-36.94, -18.67) * mm, "end": v(-36.92, -18.67) * mm});
            skLineSegment(sketch, "E383", {"start": v(-36.92, -18.67) * mm, "end": v(-36.77, -18.68) * mm});
            skLineSegment(sketch, "E384", {"start": v(-36.77, -18.68) * mm, "end": v(-36.08, -18.8) * mm});
            skLineSegment(sketch, "E385", {"start": v(-36.08, -18.8) * mm, "end": v(-35.46, -19.04) * mm});
            skLineSegment(sketch, "E386", {"start": v(-35.46, -19.04) * mm, "end": v(-35.35, -19.1) * mm});
            skLineSegment(sketch, "E387", {"start": v(-35.35, -19.1) * mm, "end": v(-35.24, -19.16) * mm});
            skLineSegment(sketch, "E388", {"start": v(-35.24, -19.16) * mm, "end": v(-34.9, -19.4) * mm});
            skLineSegment(sketch, "E389", {"start": v(-34.9, -19.4) * mm, "end": v(-34.56, -19.77) * mm});
            skLineSegment(sketch, "E390", {"start": v(-34.56, -19.77) * mm, "end": v(-34.35, -20.18) * mm});
            skLineSegment(sketch, "E391", {"start": v(-34.35, -20.18) * mm, "end": v(-34.27, -20.51) * mm});
            skLineSegment(sketch, "E392", {"start": v(-34.27, -20.51) * mm, "end": v(-34.27, -20.63) * mm});
            skLineSegment(sketch, "E393", {"start": v(-34.27, -20.63) * mm, "end": v(-34.27, -20.82) * mm});
            skLineSegment(sketch, "E394", {"start": v(-34.27, -20.82) * mm, "end": v(-34.5, -21.4) * mm});
            skLineSegment(sketch, "E395", {"start": v(-34.5, -21.4) * mm, "end": v(-35.12, -22.02) * mm});
            skLineSegment(sketch, "E396", {"start": v(-35.12, -22.02) * mm, "end": v(-36.05, -22.44) * mm});
            skLineSegment(sketch, "E397", {"start": v(-36.05, -22.44) * mm, "end": v(-36.9, -22.6) * mm});
            skLineSegment(sketch, "E398", {"start": v(-36.9, -22.6) * mm, "end": v(-37.18, -22.6) * mm});
            skLineSegment(sketch, "E399", {"start": v(-37.18, -22.6) * mm, "end": v(-37.47, -22.6) * mm});
            skLineSegment(sketch, "E400", {"start": v(-37.47, -22.6) * mm, "end": v(-38.32, -22.44) * mm});
            skLineSegment(sketch, "E401", {"start": v(-38.32, -22.44) * mm, "end": v(-39.24, -22.02) * mm});
            skLineSegment(sketch, "E402", {"start": v(-39.24, -22.02) * mm, "end": v(-39.87, -21.4) * mm});
            skLineSegment(sketch, "E403", {"start": v(-39.87, -21.4) * mm, "end": v(-40.1, -20.82) * mm});
            skLineSegment(sketch, "E404", {"start": v(-40.1, -20.82) * mm, "end": v(-40.1, -20.63) * mm});
            skLineSegment(sketch, "E405", {"start": v(-40.1, -20.63) * mm, "end": v(-40.1, -20.44) * mm});
            skLineSegment(sketch, "E406", {"start": v(-40.1, -20.44) * mm, "end": v(-39.87, -19.86) * mm});
            skLineSegment(sketch, "E407", {"start": v(-39.87, -19.86) * mm, "end": v(-39.24, -19.24) * mm});
            skLineSegment(sketch, "E408", {"start": v(-39.24, -19.24) * mm, "end": v(-38.32, -18.82) * mm});
            skLineSegment(sketch, "E409", {"start": v(-38.32, -18.82) * mm, "end": v(-37.47, -18.66) * mm});
            skLineSegment(sketch, "E410", {"start": v(-37.47, -18.66) * mm, "end": v(-37.18, -18.66) * mm});
            skLineSegment(sketch, "E411", {"start": v(-36.42, -13.38) * mm, "end": v(-36.37, -13.18) * mm});
            skLineSegment(sketch, "E412", {"start": v(-36.37, -13.18) * mm, "end": v(-36.15, -12.6) * mm});
            skLineSegment(sketch, "E413", {"start": v(-36.15, -12.6) * mm, "end": v(-35.78, -11.93) * mm});
            skLineSegment(sketch, "E414", {"start": v(-35.78, -11.93) * mm, "end": v(-35.3, -11.4) * mm});
            skLineSegment(sketch, "E415", {"start": v(-35.3, -11.4) * mm, "end": v(-34.89, -11.1) * mm});
            skLineSegment(sketch, "E416", {"start": v(-34.89, -11.1) * mm, "end": v(-34.74, -11.03) * mm});
            skLineSegment(sketch, "E417", {"start": v(-34.74, -11.03) * mm, "end": v(-34.51, -10.92) * mm});
            skLineSegment(sketch, "E418", {"start": v(-34.51, -10.92) * mm, "end": v(-33.33, -10.7) * mm});
            skLineSegment(sketch, "E419", {"start": v(-33.33, -10.7) * mm, "end": v(-32.14, -10.87) * mm});
            skLineSegment(sketch, "E420", {"start": v(-32.14, -10.87) * mm, "end": v(-31.9, -10.97) * mm});
            skLineSegment(sketch, "E421", {"start": v(-31.9, -10.97) * mm, "end": v(-31.7, -11.05) * mm});
            skLineSegment(sketch, "E422", {"start": v(-31.7, -11.05) * mm, "end": v(-31.15, -11.4) * mm});
            skLineSegment(sketch, "E423", {"start": v(-31.15, -11.4) * mm, "end": v(-30.49, -11.99) * mm});
            skLineSegment(sketch, "E424", {"start": v(-30.49, -11.99) * mm, "end": v(-29.96, -12.7) * mm});
            skLineSegment(sketch, "E425", {"start": v(-29.96, -12.7) * mm, "end": v(-29.66, -13.32) * mm});
            skLineSegment(sketch, "E426", {"start": v(-29.66, -13.32) * mm, "end": v(-29.6, -13.53) * mm});
            skLineSegment(sketch, "E427", {"start": v(-29.6, -13.53) * mm, "end": v(-29.49, -13.85) * mm});
            skLineSegment(sketch, "E428", {"start": v(-29.49, -13.85) * mm, "end": v(-29.3, -14.85) * mm});
            skLineSegment(sketch, "E429", {"start": v(-29.3, -14.85) * mm, "end": v(-29.22, -16.2) * mm});
            skLineSegment(sketch, "E430", {"start": v(-29.22, -16.2) * mm, "end": v(-29.28, -17.53) * mm});
            skLineSegment(sketch, "E431", {"start": v(-29.28, -17.53) * mm, "end": v(-29.37, -18.5) * mm});
            skLineSegment(sketch, "E432", {"start": v(-29.37, -18.5) * mm, "end": v(-29.4, -18.82) * mm});
            skLineSegment(sketch, "E433", {"start": v(-29.4, -18.82) * mm, "end": v(-29.41, -18.87) * mm});
            skLineSegment(sketch, "E434", {"start": v(-29.41, -18.87) * mm, "end": v(-29.42, -18.94) * mm});
            skLineSegment(sketch, "E435", {"start": v(-29.42, -18.94) * mm, "end": v(-29.5, -19.15) * mm});
            skLineSegment(sketch, "E436", {"start": v(-29.5, -19.15) * mm, "end": v(-29.66, -19.36) * mm});
            skLineSegment(sketch, "E437", {"start": v(-29.66, -19.36) * mm, "end": v(-29.9, -19.5) * mm});
            skLineSegment(sketch, "E438", {"start": v(-29.9, -19.5) * mm, "end": v(-30.1, -19.56) * mm});
            skLineSegment(sketch, "E439", {"start": v(-30.1, -19.56) * mm, "end": v(-30.17, -19.56) * mm});
            skLineSegment(sketch, "E440", {"start": v(-30.17, -19.56) * mm, "end": v(-30.19, -19.56) * mm});
            skLineSegment(sketch, "E441", {"start": v(-30.19, -19.56) * mm, "end": v(-30.24, -19.55) * mm});
            skLineSegment(sketch, "E442", {"start": v(-30.24, -19.55) * mm, "end": v(-30.25, -19.55) * mm});
            skLineSegment(sketch, "E443", {"start": v(-30.25, -19.55) * mm, "end": v(-30.33, -19.55) * mm});
            skLineSegment(sketch, "E444", {"start": v(-30.33, -19.55) * mm, "end": v(-30.54, -19.46) * mm});
            skLineSegment(sketch, "E445", {"start": v(-30.54, -19.46) * mm, "end": v(-30.77, -19.27) * mm});
            skLineSegment(sketch, "E446", {"start": v(-30.77, -19.27) * mm, "end": v(-30.9, -19.01) * mm});
            skLineSegment(sketch, "E447", {"start": v(-30.9, -19.01) * mm, "end": v(-30.94, -18.78) * mm});
            skLineSegment(sketch, "E448", {"start": v(-30.94, -18.78) * mm, "end": v(-30.93, -18.71) * mm});
            skLineSegment(sketch, "E449", {"start": v(-30.93, -18.71) * mm, "end": v(-30.92, -18.66) * mm});
            skLineSegment(sketch, "E450", {"start": v(-30.92, -18.66) * mm, "end": v(-30.9, -18.36) * mm});
            skLineSegment(sketch, "E451", {"start": v(-30.9, -18.36) * mm, "end": v(-30.8, -17.46) * mm});
            skLineSegment(sketch, "E452", {"start": v(-30.8, -17.46) * mm, "end": v(-30.75, -16.27) * mm});
            skLineSegment(sketch, "E453", {"start": v(-30.75, -16.27) * mm, "end": v(-30.8, -15.1) * mm});
            skLineSegment(sketch, "E454", {"start": v(-30.8, -15.1) * mm, "end": v(-30.96, -14.27) * mm});
            skLineSegment(sketch, "E455", {"start": v(-30.96, -14.27) * mm, "end": v(-31.05, -14) * mm});
            skLineSegment(sketch, "E456", {"start": v(-31.05, -14) * mm, "end": v(-31.09, -13.87) * mm});
            skLineSegment(sketch, "E457", {"start": v(-31.09, -13.87) * mm, "end": v(-31.28, -13.49) * mm});
            skLineSegment(sketch, "E458", {"start": v(-31.28, -13.49) * mm, "end": v(-31.62, -13.03) * mm});
            skLineSegment(sketch, "E459", {"start": v(-31.62, -13.03) * mm, "end": v(-32.03, -12.65) * mm});
            skLineSegment(sketch, "E460", {"start": v(-32.03, -12.65) * mm, "end": v(-32.38, -12.43) * mm});
            skLineSegment(sketch, "E461", {"start": v(-32.38, -12.43) * mm, "end": v(-32.5, -12.38) * mm});
            skLineSegment(sketch, "E462", {"start": v(-32.5, -12.38) * mm, "end": v(-32.58, -12.34) * mm});
            skLineSegment(sketch, "E463", {"start": v(-32.58, -12.34) * mm, "end": v(-32.81, -12.27) * mm});
            skLineSegment(sketch, "E464", {"start": v(-32.81, -12.27) * mm, "end": v(-33.19, -12.22) * mm});
            skLineSegment(sketch, "E465", {"start": v(-33.19, -12.22) * mm, "end": v(-33.6, -12.25) * mm});
            skLineSegment(sketch, "E466", {"start": v(-33.6, -12.25) * mm, "end": v(-33.96, -12.36) * mm});
            skLineSegment(sketch, "E467", {"start": v(-33.96, -12.36) * mm, "end": v(-34.07, -12.41) * mm});
            skLineSegment(sketch, "E468", {"start": v(-34.07, -12.41) * mm, "end": v(-34.17, -12.46) * mm});
            skLineSegment(sketch, "E469", {"start": v(-34.17, -12.46) * mm, "end": v(-34.41, -12.67) * mm});
            skLineSegment(sketch, "E470", {"start": v(-34.41, -12.67) * mm, "end": v(-34.66, -13.03) * mm});
            skLineSegment(sketch, "E471", {"start": v(-34.66, -13.03) * mm, "end": v(-34.83, -13.41) * mm});
            skLineSegment(sketch, "E472", {"start": v(-34.83, -13.41) * mm, "end": v(-34.92, -13.67) * mm});
            skLineSegment(sketch, "E473", {"start": v(-34.92, -13.67) * mm, "end": v(-34.94, -13.75) * mm});
            skLineSegment(sketch, "E474", {"start": v(-34.94, -13.75) * mm, "end": v(-35.04, -14.17) * mm});
            skLineSegment(sketch, "E475", {"start": v(-35.04, -14.17) * mm, "end": v(-35.35, -16.13) * mm});
            skLineSegment(sketch, "E476", {"start": v(-35.35, -16.13) * mm, "end": v(-35.39, -17.96) * mm});
            skLineSegment(sketch, "E477", {"start": v(-35.39, -17.96) * mm, "end": v(-35.35, -18.3) * mm});
            skLineSegment(sketch, "E478", {"start": v(-35.35, -18.3) * mm, "end": v(-35.46, -18.24) * mm});
            skLineSegment(sketch, "E479", {"start": v(-35.46, -18.24) * mm, "end": v(-36.08, -18.02) * mm});
            skLineSegment(sketch, "E480", {"start": v(-36.08, -18.02) * mm, "end": v(-36.77, -17.89) * mm});
            skLineSegment(sketch, "E481", {"start": v(-36.77, -17.89) * mm, "end": v(-36.92, -17.88) * mm});
            skLineSegment(sketch, "E482", {"start": v(-36.92, -17.88) * mm, "end": v(-36.93, -17.53) * mm});
            skLineSegment(sketch, "E483", {"start": v(-36.93, -17.53) * mm, "end": v(-36.84, -15.7) * mm});
            skLineSegment(sketch, "E484", {"start": v(-36.84, -15.7) * mm, "end": v(-36.52, -13.78) * mm});
            skLineSegment(sketch, "E485", {"start": v(-36.52, -13.78) * mm, "end": v(-36.42, -13.38) * mm});
            skLineSegment(sketch, "E486", {"start": v(-22.31, 19.2) * mm, "end": v(-22.31, 19.17) * mm});
            skLineSegment(sketch, "E487", {"start": v(-22.31, 19.17) * mm, "end": v(-22.51, 19.04) * mm});
            skLineSegment(sketch, "E488", {"start": v(-22.51, 19.04) * mm, "end": v(-23.06, 18.91) * mm});
            skLineSegment(sketch, "E489", {"start": v(-23.06, 18.91) * mm, "end": v(-23.86, 18.82) * mm});
            skLineSegment(sketch, "E490", {"start": v(-23.86, 18.82) * mm, "end": v(-24.6, 18.79) * mm});
            skLineSegment(sketch, "E491", {"start": v(-24.6, 18.79) * mm, "end": v(-24.85, 18.79) * mm});
            skLineSegment(sketch, "E492", {"start": v(-24.85, 18.79) * mm, "end": v(-25.1, 18.79) * mm});
            skLineSegment(sketch, "E493", {"start": v(-25.1, 18.79) * mm, "end": v(-25.84, 18.82) * mm});
            skLineSegment(sketch, "E494", {"start": v(-25.84, 18.82) * mm, "end": v(-26.65, 18.91) * mm});
            skLineSegment(sketch, "E495", {"start": v(-26.65, 18.91) * mm, "end": v(-27.2, 19.04) * mm});
            skLineSegment(sketch, "E496", {"start": v(-27.2, 19.04) * mm, "end": v(-27.4, 19.17) * mm});
            skLineSegment(sketch, "E497", {"start": v(-27.4, 19.17) * mm, "end": v(-27.4, 19.2) * mm});
            skLineSegment(sketch, "E498", {"start": v(-27.4, 19.2) * mm, "end": v(-27.4, 19.25) * mm});
            skLineSegment(sketch, "E499", {"start": v(-27.4, 19.25) * mm, "end": v(-27.2, 19.37) * mm});
            skLineSegment(sketch, "E500", {"start": v(-27.2, 19.37) * mm, "end": v(-26.65, 19.5) * mm});
            skLineSegment(sketch, "E501", {"start": v(-26.65, 19.5) * mm, "end": v(-25.84, 19.59) * mm});
            skLineSegment(sketch, "E502", {"start": v(-25.84, 19.59) * mm, "end": v(-25.1, 19.62) * mm});
            skLineSegment(sketch, "E503", {"start": v(-25.1, 19.62) * mm, "end": v(-24.85, 19.62) * mm});
            skLineSegment(sketch, "E504", {"start": v(-24.85, 19.62) * mm, "end": v(-24.6, 19.62) * mm});
            skLineSegment(sketch, "E505", {"start": v(-24.6, 19.62) * mm, "end": v(-23.86, 19.59) * mm});
            skLineSegment(sketch, "E506", {"start": v(-23.86, 19.59) * mm, "end": v(-23.06, 19.5) * mm});
            skLineSegment(sketch, "E507", {"start": v(-23.06, 19.5) * mm, "end": v(-22.51, 19.37) * mm});
            skLineSegment(sketch, "E508", {"start": v(-22.51, 19.37) * mm, "end": v(-22.31, 19.25) * mm});
            skLineSegment(sketch, "E509", {"start": v(-22.31, 19.25) * mm, "end": v(-22.31, 19.2) * mm});
            skLineSegment(sketch, "E510", {"start": v(-22.1, 22.12) * mm, "end": v(-22.1, 22) * mm});
            skLineSegment(sketch, "E511", {"start": v(-22.1, 22) * mm, "end": v(-22.18, 21.68) * mm});
            skLineSegment(sketch, "E512", {"start": v(-22.18, 21.68) * mm, "end": v(-22.43, 21.32) * mm});
            skLineSegment(sketch, "E513", {"start": v(-22.43, 21.32) * mm, "end": v(-22.79, 21.07) * mm});
            skLineSegment(sketch, "E514", {"start": v(-22.79, 21.07) * mm, "end": v(-23.12, 20.98) * mm});
            skLineSegment(sketch, "E515", {"start": v(-23.12, 20.98) * mm, "end": v(-23.23, 20.98) * mm});
            skLineSegment(sketch, "E516", {"start": v(-23.23, 20.98) * mm, "end": v(-23.34, 20.98) * mm});
            skLineSegment(sketch, "E517", {"start": v(-23.34, 20.98) * mm, "end": v(-23.67, 21.07) * mm});
            skLineSegment(sketch, "E518", {"start": v(-23.67, 21.07) * mm, "end": v(-24.03, 21.32) * mm});
            skLineSegment(sketch, "E519", {"start": v(-24.03, 21.32) * mm, "end": v(-24.28, 21.68) * mm});
            skLineSegment(sketch, "E520", {"start": v(-24.28, 21.68) * mm, "end": v(-24.36, 22) * mm});
            skLineSegment(sketch, "E521", {"start": v(-24.36, 22) * mm, "end": v(-24.36, 22.12) * mm});
            skLineSegment(sketch, "E522", {"start": v(-24.36, 22.12) * mm, "end": v(-24.36, 22.23) * mm});
            skLineSegment(sketch, "E523", {"start": v(-24.36, 22.23) * mm, "end": v(-24.28, 22.56) * mm});
            skLineSegment(sketch, "E524", {"start": v(-24.28, 22.56) * mm, "end": v(-24.03, 22.92) * mm});
            skLineSegment(sketch, "E525", {"start": v(-24.03, 22.92) * mm, "end": v(-23.67, 23.16) * mm});
            skLineSegment(sketch, "E526", {"start": v(-23.67, 23.16) * mm, "end": v(-23.34, 23.25) * mm});
            skLineSegment(sketch, "E527", {"start": v(-23.34, 23.25) * mm, "end": v(-23.23, 23.25) * mm});
            skLineSegment(sketch, "E528", {"start": v(-23.23, 23.25) * mm, "end": v(-23.12, 23.25) * mm});
            skLineSegment(sketch, "E529", {"start": v(-23.12, 23.25) * mm, "end": v(-22.79, 23.16) * mm});
            skLineSegment(sketch, "E530", {"start": v(-22.79, 23.16) * mm, "end": v(-22.43, 22.92) * mm});
            skLineSegment(sketch, "E531", {"start": v(-22.43, 22.92) * mm, "end": v(-22.18, 22.56) * mm});
            skLineSegment(sketch, "E532", {"start": v(-22.18, 22.56) * mm, "end": v(-22.1, 22.23) * mm});
            skLineSegment(sketch, "E533", {"start": v(-22.1, 22.23) * mm, "end": v(-22.1, 22.12) * mm});
            skLineSegment(sketch, "E534", {"start": v(-25.24, 39.73) * mm, "end": v(-25.24, 39.64) * mm});
            skLineSegment(sketch, "E535", {"start": v(-25.24, 39.64) * mm, "end": v(-25.31, 39.39) * mm});
            skLineSegment(sketch, "E536", {"start": v(-25.31, 39.39) * mm, "end": v(-25.5, 39.1) * mm});
            skLineSegment(sketch, "E537", {"start": v(-25.5, 39.1) * mm, "end": v(-25.78, 38.92) * mm});
            skLineSegment(sketch, "E538", {"start": v(-25.78, 38.92) * mm, "end": v(-26.04, 38.85) * mm});
            skLineSegment(sketch, "E539", {"start": v(-26.04, 38.85) * mm, "end": v(-26.13, 38.85) * mm});
            skLineSegment(sketch, "E540", {"start": v(-26.13, 38.85) * mm, "end": v(-26.21, 38.85) * mm});
            skLineSegment(sketch, "E541", {"start": v(-26.21, 38.85) * mm, "end": v(-26.47, 38.92) * mm});
            skLineSegment(sketch, "E542", {"start": v(-26.47, 38.92) * mm, "end": v(-26.75, 39.1) * mm});
            skLineSegment(sketch, "E543", {"start": v(-26.75, 39.1) * mm, "end": v(-26.94, 39.39) * mm});
            skLineSegment(sketch, "E544", {"start": v(-26.94, 39.39) * mm, "end": v(-27, 39.64) * mm});
            skLineSegment(sketch, "E545", {"start": v(-27, 39.64) * mm, "end": v(-27, 39.73) * mm});
            skLineSegment(sketch, "E546", {"start": v(-27, 39.73) * mm, "end": v(-27, 39.82) * mm});
            skLineSegment(sketch, "E547", {"start": v(-27, 39.82) * mm, "end": v(-26.94, 40.07) * mm});
            skLineSegment(sketch, "E548", {"start": v(-26.94, 40.07) * mm, "end": v(-26.75, 40.35) * mm});
            skLineSegment(sketch, "E549", {"start": v(-26.75, 40.35) * mm, "end": v(-26.47, 40.54) * mm});
            skLineSegment(sketch, "E550", {"start": v(-26.47, 40.54) * mm, "end": v(-26.21, 40.61) * mm});
            skLineSegment(sketch, "E551", {"start": v(-26.21, 40.61) * mm, "end": v(-26.13, 40.61) * mm});
            skLineSegment(sketch, "E552", {"start": v(-26.13, 40.61) * mm, "end": v(-26.04, 40.61) * mm});
            skLineSegment(sketch, "E553", {"start": v(-26.04, 40.61) * mm, "end": v(-25.78, 40.54) * mm});
            skLineSegment(sketch, "E554", {"start": v(-25.78, 40.54) * mm, "end": v(-25.5, 40.35) * mm});
            skLineSegment(sketch, "E555", {"start": v(-25.5, 40.35) * mm, "end": v(-25.31, 40.07) * mm});
            skLineSegment(sketch, "E556", {"start": v(-25.31, 40.07) * mm, "end": v(-25.24, 39.82) * mm});
            skLineSegment(sketch, "E557", {"start": v(-25.24, 39.82) * mm, "end": v(-25.24, 39.73) * mm});
            skLineSegment(sketch, "E558", {"start": v(-20.97, 26.54) * mm, "end": v(-20.97, 26.4) * mm});
            skLineSegment(sketch, "E559", {"start": v(-20.97, 26.4) * mm, "end": v(-21.08, 25.97) * mm});
            skLineSegment(sketch, "E560", {"start": v(-21.08, 25.97) * mm, "end": v(-21.4, 25.5) * mm});
            skLineSegment(sketch, "E561", {"start": v(-21.4, 25.5) * mm, "end": v(-21.86, 25.2) * mm});
            skLineSegment(sketch, "E562", {"start": v(-21.86, 25.2) * mm, "end": v(-22.28, 25.08) * mm});
            skLineSegment(sketch, "E563", {"start": v(-22.28, 25.08) * mm, "end": v(-22.43, 25.08) * mm});
            skLineSegment(sketch, "E564", {"start": v(-22.43, 25.08) * mm, "end": v(-22.57, 25.08) * mm});
            skLineSegment(sketch, "E565", {"start": v(-22.57, 25.08) * mm, "end": v(-23, 25.2) * mm});
            skLineSegment(sketch, "E566", {"start": v(-23, 25.2) * mm, "end": v(-23.46, 25.5) * mm});
            skLineSegment(sketch, "E567", {"start": v(-23.46, 25.5) * mm, "end": v(-23.77, 25.97) * mm});
            skLineSegment(sketch, "E568", {"start": v(-23.77, 25.97) * mm, "end": v(-23.88, 26.4) * mm});
            skLineSegment(sketch, "E569", {"start": v(-23.88, 26.4) * mm, "end": v(-23.88, 26.54) * mm});
            skLineSegment(sketch, "E570", {"start": v(-23.88, 26.54) * mm, "end": v(-23.88, 26.68) * mm});
            skLineSegment(sketch, "E571", {"start": v(-23.88, 26.68) * mm, "end": v(-23.77, 27.1) * mm});
            skLineSegment(sketch, "E572", {"start": v(-23.77, 27.1) * mm, "end": v(-23.46, 27.57) * mm});
            skLineSegment(sketch, "E573", {"start": v(-23.46, 27.57) * mm, "end": v(-23, 27.88) * mm});
            skLineSegment(sketch, "E574", {"start": v(-23, 27.88) * mm, "end": v(-22.57, 28) * mm});
            skLineSegment(sketch, "E575", {"start": v(-22.57, 28) * mm, "end": v(-22.43, 28) * mm});
            skLineSegment(sketch, "E576", {"start": v(-22.43, 28) * mm, "end": v(-22.28, 28) * mm});
            skLineSegment(sketch, "E577", {"start": v(-22.28, 28) * mm, "end": v(-21.86, 27.88) * mm});
            skLineSegment(sketch, "E578", {"start": v(-21.86, 27.88) * mm, "end": v(-21.4, 27.57) * mm});
            skLineSegment(sketch, "E579", {"start": v(-21.4, 27.57) * mm, "end": v(-21.08, 27.1) * mm});
            skLineSegment(sketch, "E580", {"start": v(-21.08, 27.1) * mm, "end": v(-20.97, 26.68) * mm});
            skLineSegment(sketch, "E581", {"start": v(-20.97, 26.68) * mm, "end": v(-20.97, 26.54) * mm});
            skLineSegment(sketch, "E582", {"start": v(-23.73, 30.72) * mm, "end": v(-23.73, 30.6) * mm});
            skLineSegment(sketch, "E583", {"start": v(-23.73, 30.6) * mm, "end": v(-23.83, 30.23) * mm});
            skLineSegment(sketch, "E584", {"start": v(-23.83, 30.23) * mm, "end": v(-24.1, 29.82) * mm});
            skLineSegment(sketch, "E585", {"start": v(-24.1, 29.82) * mm, "end": v(-24.5, 29.55) * mm});
            skLineSegment(sketch, "E586", {"start": v(-24.5, 29.55) * mm, "end": v(-24.88, 29.45) * mm});
            skLineSegment(sketch, "E587", {"start": v(-24.88, 29.45) * mm, "end": v(-25, 29.45) * mm});
            skLineSegment(sketch, "E588", {"start": v(-25, 29.45) * mm, "end": v(-25.13, 29.45) * mm});
            skLineSegment(sketch, "E589", {"start": v(-25.13, 29.45) * mm, "end": v(-25.5, 29.55) * mm});
            skLineSegment(sketch, "E590", {"start": v(-25.5, 29.55) * mm, "end": v(-25.9, 29.82) * mm});
            skLineSegment(sketch, "E591", {"start": v(-25.9, 29.82) * mm, "end": v(-26.18, 30.23) * mm});
            skLineSegment(sketch, "E592", {"start": v(-26.18, 30.23) * mm, "end": v(-26.28, 30.6) * mm});
            skLineSegment(sketch, "E593", {"start": v(-26.28, 30.6) * mm, "end": v(-26.28, 30.72) * mm});
            skLineSegment(sketch, "E594", {"start": v(-26.28, 30.72) * mm, "end": v(-26.28, 30.84) * mm});
            skLineSegment(sketch, "E595", {"start": v(-26.28, 30.84) * mm, "end": v(-26.18, 31.22) * mm});
            skLineSegment(sketch, "E596", {"start": v(-26.18, 31.22) * mm, "end": v(-25.9, 31.62) * mm});
            skLineSegment(sketch, "E597", {"start": v(-25.9, 31.62) * mm, "end": v(-25.5, 31.9) * mm});
            skLineSegment(sketch, "E598", {"start": v(-25.5, 31.9) * mm, "end": v(-25.13, 32) * mm});
            skLineSegment(sketch, "E599", {"start": v(-25.13, 32) * mm, "end": v(-25, 32) * mm});
            skLineSegment(sketch, "E600", {"start": v(-25, 32) * mm, "end": v(-24.88, 32) * mm});
            skLineSegment(sketch, "E601", {"start": v(-24.88, 32) * mm, "end": v(-24.5, 31.9) * mm});
            skLineSegment(sketch, "E602", {"start": v(-24.5, 31.9) * mm, "end": v(-24.1, 31.62) * mm});
            skLineSegment(sketch, "E603", {"start": v(-24.1, 31.62) * mm, "end": v(-23.83, 31.22) * mm});
            skLineSegment(sketch, "E604", {"start": v(-23.83, 31.22) * mm, "end": v(-23.73, 30.84) * mm});
            skLineSegment(sketch, "E605", {"start": v(-23.73, 30.84) * mm, "end": v(-23.73, 30.72) * mm});
            skLineSegment(sketch, "E606", {"start": v(-24.83, 25.41) * mm, "end": v(-24.83, 25.16) * mm});
            skLineSegment(sketch, "E607", {"start": v(-24.83, 25.16) * mm, "end": v(-25.04, 24.41) * mm});
            skLineSegment(sketch, "E608", {"start": v(-25.04, 24.41) * mm, "end": v(-25.59, 23.6) * mm});
            skLineSegment(sketch, "E609", {"start": v(-25.59, 23.6) * mm, "end": v(-26.4, 23.04) * mm});
            skLineSegment(sketch, "E610", {"start": v(-26.4, 23.04) * mm, "end": v(-27.16, 22.84) * mm});
            skLineSegment(sketch, "E611", {"start": v(-27.16, 22.84) * mm, "end": v(-27.41, 22.84) * mm});
            skLineSegment(sketch, "E612", {"start": v(-27.41, 22.84) * mm, "end": v(-27.66, 22.84) * mm});
            skLineSegment(sketch, "E613", {"start": v(-27.66, 22.84) * mm, "end": v(-28.41, 23.04) * mm});
            skLineSegment(sketch, "E614", {"start": v(-28.41, 23.04) * mm, "end": v(-29.23, 23.6) * mm});
            skLineSegment(sketch, "E615", {"start": v(-29.23, 23.6) * mm, "end": v(-29.79, 24.41) * mm});
            skLineSegment(sketch, "E616", {"start": v(-29.79, 24.41) * mm, "end": v(-29.99, 25.16) * mm});
            skLineSegment(sketch, "E617", {"start": v(-29.99, 25.16) * mm, "end": v(-29.99, 25.41) * mm});
            skLineSegment(sketch, "E618", {"start": v(-29.99, 25.41) * mm, "end": v(-29.99, 25.66) * mm});
            skLineSegment(sketch, "E619", {"start": v(-29.99, 25.66) * mm, "end": v(-29.79, 26.42) * mm});
            skLineSegment(sketch, "E620", {"start": v(-29.79, 26.42) * mm, "end": v(-29.23, 27.24) * mm});
            skLineSegment(sketch, "E621", {"start": v(-29.23, 27.24) * mm, "end": v(-28.41, 27.79) * mm});
            skLineSegment(sketch, "E622", {"start": v(-28.41, 27.79) * mm, "end": v(-27.66, 28) * mm});
            skLineSegment(sketch, "E623", {"start": v(-27.66, 28) * mm, "end": v(-27.41, 28) * mm});
            skLineSegment(sketch, "E624", {"start": v(-27.41, 28) * mm, "end": v(-27.16, 28) * mm});
            skLineSegment(sketch, "E625", {"start": v(-27.16, 28) * mm, "end": v(-26.4, 27.79) * mm});
            skLineSegment(sketch, "E626", {"start": v(-26.4, 27.79) * mm, "end": v(-25.59, 27.24) * mm});
            skLineSegment(sketch, "E627", {"start": v(-25.59, 27.24) * mm, "end": v(-25.04, 26.42) * mm});
            skLineSegment(sketch, "E628", {"start": v(-25.04, 26.42) * mm, "end": v(-24.83, 25.66) * mm});
            skLineSegment(sketch, "E629", {"start": v(-24.83, 25.66) * mm, "end": v(-24.83, 25.41) * mm});
            skLineSegment(sketch, "E630", {"start": v(-19.85, 36.03) * mm, "end": v(-19.85, 35.78) * mm});
            skLineSegment(sketch, "E631", {"start": v(-19.85, 35.78) * mm, "end": v(-20.05, 35.02) * mm});
            skLineSegment(sketch, "E632", {"start": v(-20.05, 35.02) * mm, "end": v(-20.6, 34.2) * mm});
            skLineSegment(sketch, "E633", {"start": v(-20.6, 34.2) * mm, "end": v(-21.42, 33.65) * mm});
            skLineSegment(sketch, "E634", {"start": v(-21.42, 33.65) * mm, "end": v(-22.18, 33.45) * mm});
            skLineSegment(sketch, "E635", {"start": v(-22.18, 33.45) * mm, "end": v(-22.43, 33.45) * mm});
            skLineSegment(sketch, "E636", {"start": v(-22.43, 33.45) * mm, "end": v(-22.68, 33.45) * mm});
            skLineSegment(sketch, "E637", {"start": v(-22.68, 33.45) * mm, "end": v(-23.43, 33.65) * mm});
            skLineSegment(sketch, "E638", {"start": v(-23.43, 33.65) * mm, "end": v(-24.25, 34.2) * mm});
            skLineSegment(sketch, "E639", {"start": v(-24.25, 34.2) * mm, "end": v(-24.8, 35.02) * mm});
            skLineSegment(sketch, "E640", {"start": v(-24.8, 35.02) * mm, "end": v(-25, 35.78) * mm});
            skLineSegment(sketch, "E641", {"start": v(-25, 35.78) * mm, "end": v(-25, 36.03) * mm});
            skLineSegment(sketch, "E642", {"start": v(-25, 36.03) * mm, "end": v(-25, 36.28) * mm});
            skLineSegment(sketch, "E643", {"start": v(-25, 36.28) * mm, "end": v(-24.8, 37.03) * mm});
            skLineSegment(sketch, "E644", {"start": v(-24.8, 37.03) * mm, "end": v(-24.25, 37.85) * mm});
            skLineSegment(sketch, "E645", {"start": v(-24.25, 37.85) * mm, "end": v(-23.43, 38.4) * mm});
            skLineSegment(sketch, "E646", {"start": v(-23.43, 38.4) * mm, "end": v(-22.68, 38.6) * mm});
            skLineSegment(sketch, "E647", {"start": v(-22.68, 38.6) * mm, "end": v(-22.43, 38.6) * mm});
            skLineSegment(sketch, "E648", {"start": v(-22.43, 38.6) * mm, "end": v(-22.18, 38.6) * mm});
            skLineSegment(sketch, "E649", {"start": v(-22.18, 38.6) * mm, "end": v(-21.42, 38.4) * mm});
            skLineSegment(sketch, "E650", {"start": v(-21.42, 38.4) * mm, "end": v(-20.6, 37.85) * mm});
            skLineSegment(sketch, "E651", {"start": v(-20.6, 37.85) * mm, "end": v(-20.05, 37.03) * mm});
            skLineSegment(sketch, "E652", {"start": v(-20.05, 37.03) * mm, "end": v(-19.85, 36.28) * mm});
            skLineSegment(sketch, "E653", {"start": v(-19.85, 36.28) * mm, "end": v(-19.85, 36.03) * mm});
            skLineSegment(sketch, "E654", {"start": v(-41.57, -26.94) * mm, "end": v(-41.57, -40.61) * mm});
            skLineSegment(sketch, "E655", {"start": v(-41.57, -40.61) * mm, "end": v(-41.57, -26.94) * mm});
            skLineSegment(sketch, "E656", {"start": v(-37.64, -26.86) * mm, "end": v(-37.64, -40.61) * mm});
            skLineSegment(sketch, "E657", {"start": v(-37.64, -40.61) * mm, "end": v(-37.64, -26.86) * mm});
            skLineSegment(sketch, "E658", {"start": v(-33.71, -26.78) * mm, "end": v(-33.71, -40.61) * mm});
            skLineSegment(sketch, "E659", {"start": v(-33.71, -40.61) * mm, "end": v(-33.71, -26.78) * mm});
            skLineSegment(sketch, "E660", {"start": v(-29.79, -26.7) * mm, "end": v(-29.79, -40.61) * mm});
            skLineSegment(sketch, "E661", {"start": v(-29.79, -40.61) * mm, "end": v(-29.79, -26.7) * mm});
            skLineSegment(sketch, "E662", {"start": v(-25.86, -26.62) * mm, "end": v(-25.86, -40.61) * mm});
            skLineSegment(sketch, "E663", {"start": v(-25.86, -40.61) * mm, "end": v(-25.86, -26.62) * mm});
            skLineSegment(sketch, "E664", {"start": v(-21.93, -26.54) * mm, "end": v(-21.93, -40.61) * mm});
            skLineSegment(sketch, "E665", {"start": v(-21.93, -40.61) * mm, "end": v(-21.93, -26.54) * mm});
            skLineSegment(sketch, "E666", {"start": v(-18, -26.46) * mm, "end": v(-18, -40.61) * mm});
            skLineSegment(sketch, "E667", {"start": v(-18, -40.61) * mm, "end": v(-18, -26.46) * mm});
            skLineSegment(sketch, "E668", {"start": v(-14.07, -26.38) * mm, "end": v(-14.07, -40.61) * mm});
            skLineSegment(sketch, "E669", {"start": v(-14.07, -40.61) * mm, "end": v(-14.07, -26.38) * mm});
            skLineSegment(sketch, "E670", {"start": v(-10.14, -26.3) * mm, "end": v(-10.14, -40.61) * mm});
            skLineSegment(sketch, "E671", {"start": v(-10.14, -40.61) * mm, "end": v(-10.14, -26.3) * mm});
            skLineSegment(sketch, "E672", {"start": v(-6.22, -26.22) * mm, "end": v(-6.22, -40.61) * mm});
            skLineSegment(sketch, "E673", {"start": v(-6.22, -40.61) * mm, "end": v(-6.22, -26.22) * mm});
            skLineSegment(sketch, "E674", {"start": v(-2.29, -26.15) * mm, "end": v(-2.29, -40.61) * mm});
            skLineSegment(sketch, "E675", {"start": v(-2.29, -40.61) * mm, "end": v(-2.29, -26.15) * mm});
            skLineSegment(sketch, "E676", {"start": v(1.64, -26.07) * mm, "end": v(1.64, -40.61) * mm});
            skLineSegment(sketch, "E677", {"start": v(1.64, -40.61) * mm, "end": v(1.64, -26.07) * mm});
            skSolve(sketch);
        }
        {
            var Q0;
            Q0=makeQuery(id+"F0.imprint","IMPRINT",FACE,{"disambiguationData":[TD([[makeQuery(id+"F0.imprint","IMPRINT",EDGE,{"derivedFrom":sQuery(id+"F0.wireOp",EDGE,"E0")}),-1.0]])]});
            var Q1;
            Q1=makeQuery(id+"F0.imprint","IMPRINT",FACE,{"disambiguationData":[TD([[makeQuery(id+"F0.imprint","IMPRINT",EDGE,{"derivedFrom":sQuery(id+"F0.wireOp",EDGE,"E510")}),-1.0]])]});
            var Q2;
            Q2=makeQuery(id+"F0.imprint","IMPRINT",FACE,{"disambiguationData":[TD([[makeQuery(id+"F0.imprint","IMPRINT",EDGE,{"derivedFrom":sQuery(id+"F0.wireOp",EDGE,"E486")}),-1.0]])]});
            var Q3;
            {var subQ0=sQuery(id+"F0.wireOp",EDGE,"E609");Q3=makeQuery(id+"F0.imprint","IMPRINT",FACE,{"disambiguationData":[TD([[makeQuery(id+"F0.imprint","IMPRINT",EDGE,{"derivedFrom":subQ0}),-1.0]])]});}
            var Q4;
            {var subQ8=sQuery(id+"F0.wireOp",EDGE,"E189");Q4=makeQuery(id+"F0.imprint","IMPRINT",FACE,{"disambiguationData":[TD([[makeQuery(id+"F0.imprint","IMPRINT",EDGE,{"derivedFrom":subQ8}),-1.0]])]});}
            var Q5;
            {var subQ9=sQuery(id+"F0.wireOp",EDGE,"E254");Q5=makeQuery(id+"F0.imprint","IMPRINT",FACE,{"disambiguationData":[TD([[makeQuery(id+"F0.imprint","IMPRINT",EDGE,{"derivedFrom":subQ9}),1.0]])]});}
            var Q6;
            {var subQ1=sQuery(id+"F0.wireOp",EDGE,"E186");var subQ6=sQuery(id+"F0.wireOp",EDGE,"E187");var subQ10=makeQuery(id+"F0.imprint","INTERSECT",VERTEX,{"derivedFrom":[subQ1,subQ6]});Q6=makeQuery(id+"F0.imprint","IMPRINT",FACE,{"disambiguationData":[TD([[makeQuery(id+"F0.imprint","IMPRINT",EDGE,{"disambiguationData":[TD([[subQ10,1.0]])],"derivedFrom":subQ1}),-1.0]])]});}
            var Q7;
            {var subQ0=sQuery(id+"F0.wireOp",EDGE,"E251");Q7=makeQuery(id+"F0.imprint","IMPRINT",FACE,{"disambiguationData":[TD([[makeQuery(id+"F0.imprint","IMPRINT",EDGE,{"derivedFrom":subQ0}),1.0]])]});}
            var Q8;
            {var subQ1=sQuery(id+"F0.wireOp",EDGE,"E186");var subQ5=sQuery(id+"F0.wireOp",EDGE,"E185");var subQ6=makeQuery(id+"F0.imprint","INTERSECT",VERTEX,{"derivedFrom":[subQ5,subQ1]});Q8=makeQuery(id+"F0.imprint","IMPRINT",FACE,{"disambiguationData":[TD([[makeQuery(id+"F0.imprint","IMPRINT",EDGE,{"disambiguationData":[TD([[subQ6,1.0]])],"derivedFrom":subQ5}),-1.0]])]});}
            var Q9;
            {var subQ12=sQuery(id+"F0.wireOp",EDGE,"E247");Q9=makeQuery(id+"F0.imprint","IMPRINT",FACE,{"disambiguationData":[TD([[makeQuery(id+"F0.imprint","IMPRINT",EDGE,{"derivedFrom":subQ12}),1.0]])]});}
            var Q10;
            {var subQ12=sQuery(id+"F0.wireOp",EDGE,"E244");Q10=makeQuery(id+"F0.imprint","IMPRINT",FACE,{"disambiguationData":[TD([[makeQuery(id+"F0.imprint","IMPRINT",EDGE,{"derivedFrom":subQ12}),1.0]])]});}
            var Q11;
            {var subQ1=sQuery(id+"F0.wireOp",EDGE,"E192");var subQ5=sQuery(id+"F0.wireOp",EDGE,"E191");var subQ6=makeQuery(id+"F0.imprint","INTERSECT",VERTEX,{"derivedFrom":[subQ5,subQ1]});Q11=makeQuery(id+"F0.imprint","IMPRINT",FACE,{"disambiguationData":[TD([[makeQuery(id+"F0.imprint","IMPRINT",EDGE,{"disambiguationData":[TD([[subQ6,1.0]])],"derivedFrom":subQ5}),-1.0]])]});}
            var Q12;
            {var subQ5=sQuery(id+"F0.wireOp",EDGE,"E193");Q12=makeQuery(id+"F0.imprint","IMPRINT",FACE,{"disambiguationData":[TD([[makeQuery(id+"F0.imprint","IMPRINT",EDGE,{"derivedFrom":subQ5}),-1.0]])]});}
            var Q13;
            {var subQ6=sQuery(id+"F0.wireOp",EDGE,"E195");Q13=makeQuery(id+"F0.imprint","IMPRINT",FACE,{"disambiguationData":[TD([[makeQuery(id+"F0.imprint","IMPRINT",EDGE,{"derivedFrom":subQ6}),-1.0]])]});}
            var Q14;
            {var subQ8=sQuery(id+"F0.wireOp",EDGE,"E197");Q14=makeQuery(id+"F0.imprint","IMPRINT",FACE,{"disambiguationData":[TD([[makeQuery(id+"F0.imprint","IMPRINT",EDGE,{"derivedFrom":subQ8}),-1.0]])]});}
            extrude(context, id + "F1", {"entities" : qUnion([Q0, Q1, Q2, Q3, Q4, Q5, Q6, Q7, Q8, Q9, Q10, Q11, Q12, Q13, Q14]), "depth" : 25 * mm, "offsetDistance" : 25 * mm});
        }
    });
